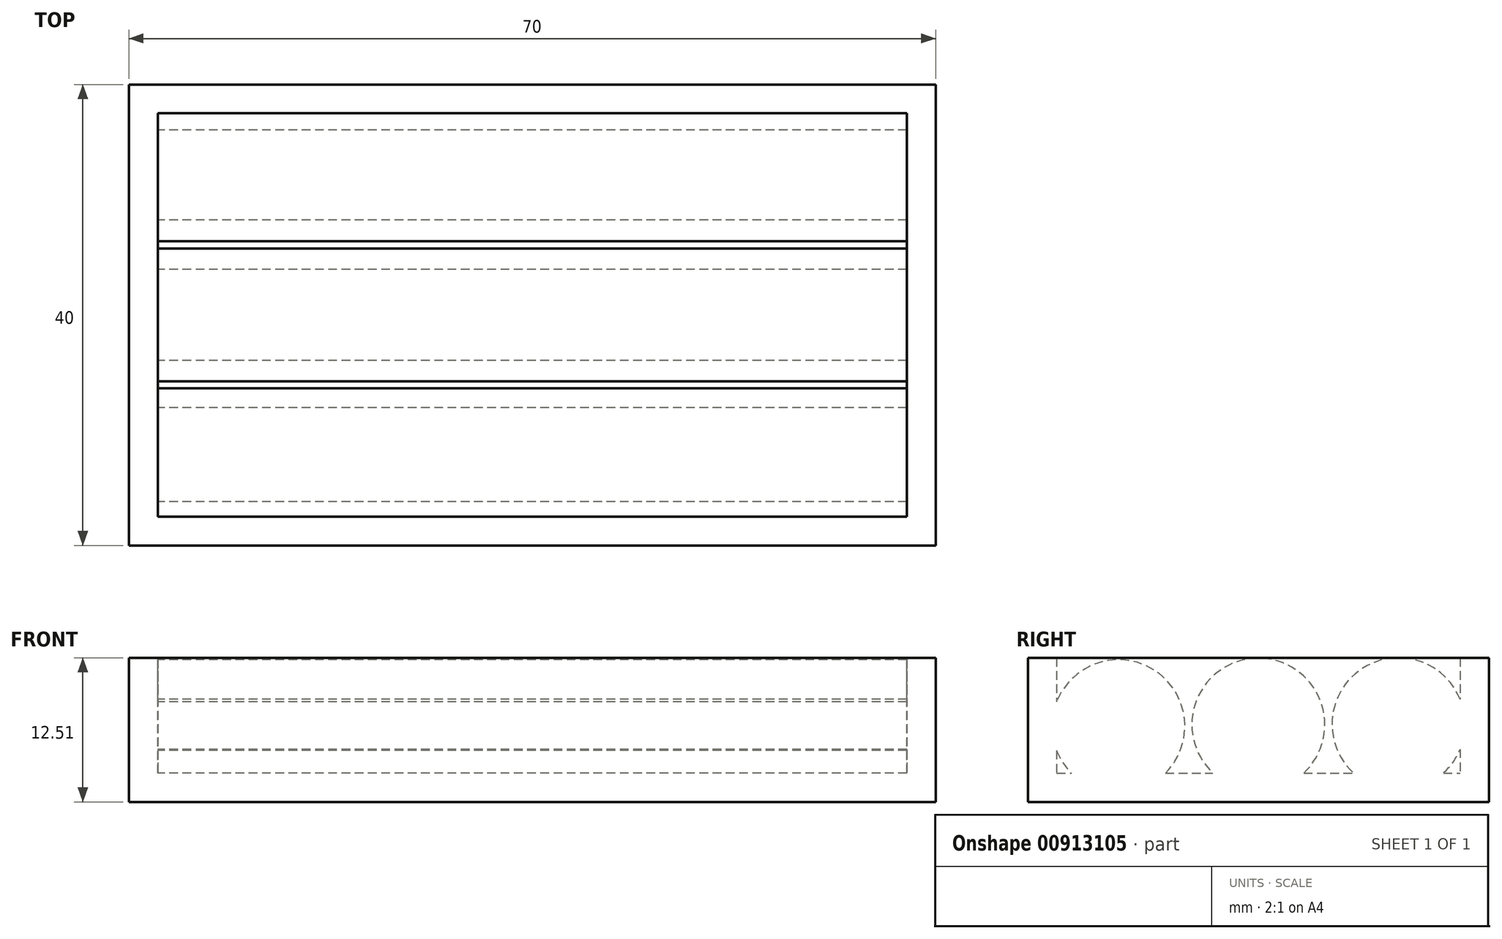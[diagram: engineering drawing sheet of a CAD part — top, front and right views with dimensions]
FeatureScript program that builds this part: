
annotation { "Feature Type Name" : "Feature", "Feature Type Description" : "" }
export const myFeature = defineFeature(function(context is Context, id is Id, definition is map)
    precondition{}
    {
        {
            var Q0;
            Q0=qCreatedBy(makeId("Top.planeOp"),FACE);
            var sketch = newSketch(context, id + "F0", { "sketchPlane" : qUnion([Q0])});
            skLineSegment(sketch, "E0.bottom", {"start": v(35, -20) * mm, "end": v(-35, -20) * mm});
            skLineSegment(sketch, "E0.top", {"start": v(35, 20) * mm, "end": v(-35, 20) * mm});
            skLineSegment(sketch, "E0.left", {"start": v(35, -20) * mm, "end": v(35, 20) * mm});
            skLineSegment(sketch, "E0.right", {"start": v(-35, -20) * mm, "end": v(-35, 20) * mm});
            skPoint(sketch, "E0.middle", {"position": v(0, 0) * mm});
            skSolve(sketch);
        }
        {
            var Q0;
            Q0 = qSketchRegion(id + "F0", true);
            extrude(context, id + "F1", {"entities" : qUnion([Q0]), "depth" : 12.5 * mm, "offsetDistance" : 25 * mm});
        }
        {
            var Q0;
            Q0=makeQuery(id+"F1.opExtrude","CAP_FACE",FACE,{"disambiguationData":[OSD([sQuery(id+"F0.wireOp",EDGE,"E0.bottom"),sQuery(id+"F0.wireOp",EDGE,"E0.top"),sQuery(id+"F0.wireOp",EDGE,"E0.left"),sQuery(id+"F0.wireOp",EDGE,"E0.right")])],"isStart":false});
            shell(context, id + "F2", {"entities" : qUnion([Q0]), "thickness" : 2.5 * mm});
        }
        {
            var Q0;
            Q0=qCreatedBy(makeId("Right.planeOp"),FACE);
            cPlane(context, id + "F3", {"entities" : qUnion([Q0]), "cplaneType" : CPlaneType.OFFSET, "offset" : 32.5 * mm, "oppositeDirection" : true, "width" : 150 * mm, "height" : 150 * mm});
        }
        {
            var Q0;
            Q0=qCreatedBy(id+"F3.planeOp",FACE);
            var sketch = newSketch(context, id + "F4", { "sketchPlane" : qUnion([Q0])});
            skCircle(sketch, "E1", {"center": v(0, 6.7) * mm, "radius": 5.77 * mm});
            skCircle(sketch, "E2", {"center": v(12.16, 6.74) * mm, "radius": 5.77 * mm});
            skCircle(sketch, "E3", {"center": v(-12.14, 6.57) * mm, "radius": 5.77 * mm});
            skSolve(sketch);
        }
        {
            var Q0;
            Q0 = qSketchRegion(id + "F4", true);
            extrude(context, id + "F5", {"entities" : qUnion([Q0]), "operationType" : NewBodyOperationType.ADD, "depth" : 65 * mm, "offsetDistance" : 25 * mm});
        }
    });
